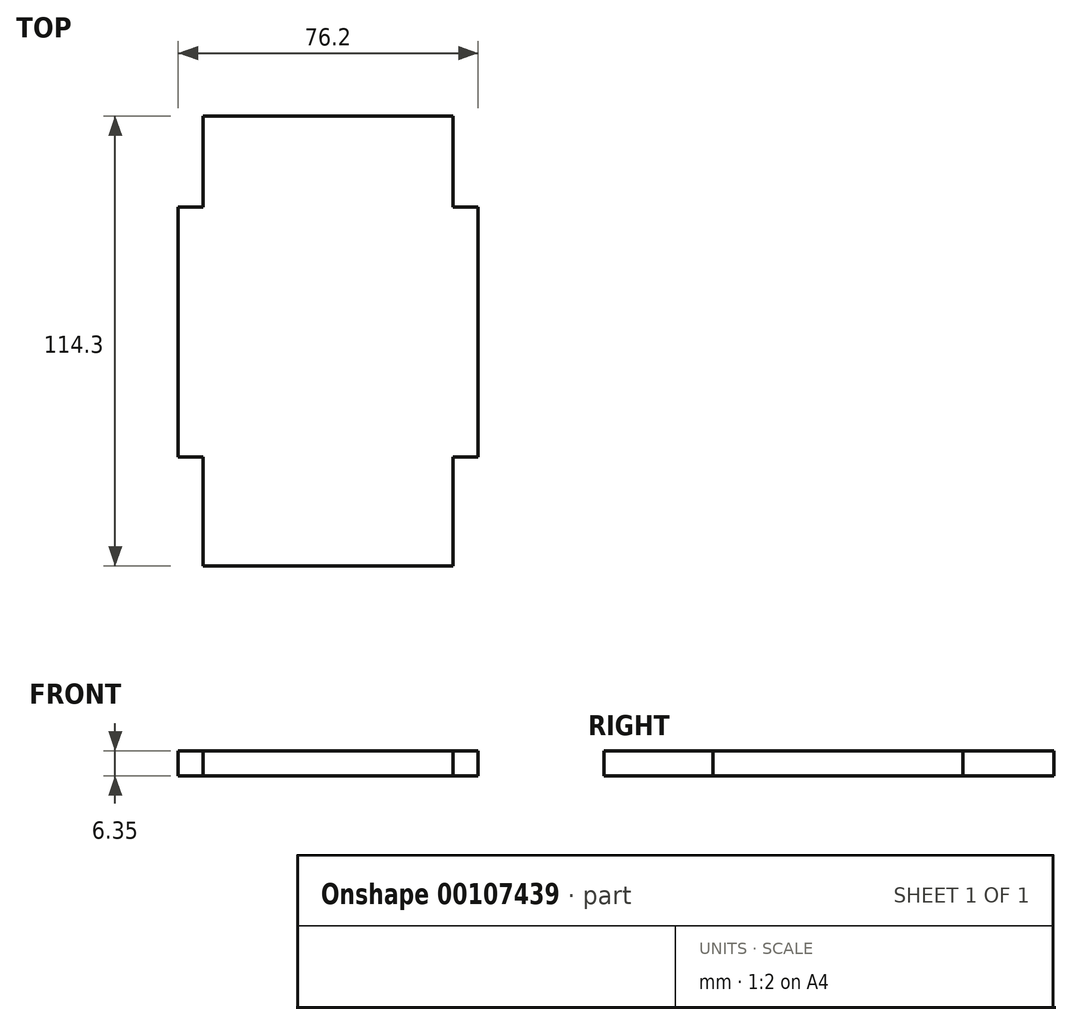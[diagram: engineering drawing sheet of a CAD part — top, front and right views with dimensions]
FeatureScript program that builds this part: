
annotation { "Feature Type Name" : "Feature", "Feature Type Description" : "" }
export const myFeature = defineFeature(function(context is Context, id is Id, definition is map)
    precondition{}
    {
        {
            var Q0;
            Q0=qCreatedBy(makeId("Top.planeOp"),FACE);
            var sketch = newSketch(context, id + "F0", { "sketchPlane" : qUnion([Q0])});
            skLineSegment(sketch, "E0.bottom", {"start": v(-39.15, 48.23) * mm, "end": v(24.35, 48.23) * mm});
            skLineSegment(sketch, "E0.top", {"start": v(-39.15, -66.07) * mm, "end": v(24.35, -66.07) * mm});
            skLineSegment(sketch, "E0.left", {"start": v(-39.15, 48.23) * mm, "end": v(-39.15, -66.07) * mm});
            skLineSegment(sketch, "E0.right", {"start": v(24.35, 48.23) * mm, "end": v(24.35, -66.07) * mm});
            skLineSegment(sketch, "E1", {"start": v(-39.15, 25.11) * mm, "end": v(-45.5, 25.11) * mm});
            skLineSegment(sketch, "E2", {"start": v(-45.5, 25.11) * mm, "end": v(-45.5, -38.39) * mm});
            skLineSegment(sketch, "E3", {"start": v(-45.5, -38.39) * mm, "end": v(-39.15, -38.39) * mm});
            skLineSegment(sketch, "E4", {"start": v(24.35, 25.11) * mm, "end": v(30.7, 25.11) * mm});
            skLineSegment(sketch, "E5", {"start": v(30.7, 25.11) * mm, "end": v(30.7, -38.39) * mm});
            skLineSegment(sketch, "E6", {"start": v(30.7, -38.39) * mm, "end": v(24.35, -38.39) * mm});
            skSolve(sketch);
        }
        {
            var Q0;
            Q0 = qSketchRegion(id + "F0", true);
            extrude(context, id + "F1", {"entities" : qUnion([Q0]), "depth" : 6.35 * mm});
        }
    });
